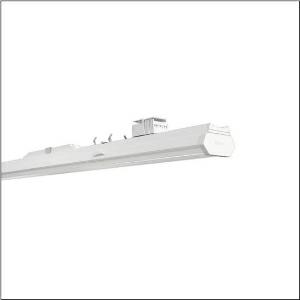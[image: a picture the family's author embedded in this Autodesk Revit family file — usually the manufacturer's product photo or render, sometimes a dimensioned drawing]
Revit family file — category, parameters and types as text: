
# Revit family: licross_21_protected_ho_52tp11dn4axs
name_source: partatom
category: Lighting Fixtures
units: mm (PartAtom-declared; Revit-internal decimal feet)

## family parameters
Cut with Voids When Loaded = No
Host = Face
Light Source = No
Part Type = Normal
Room Calculation Point = No
Round Connector Dimension = Use Diameter
Shared = No

## types (1)
- --- (1 x LED, 10000 lm, 55.1 W, 4000K)
    Apparent Load = 55 VA
    CIE Flux Codes = 84 94 98 99 100
    Color Rendering = 80
    Color Temperature = 4000K
    Default Elevation = 1800 mm
    Description = Licross 21 Protected HO, luminaire insert, of sheet steel, galvanised, coil coated, white, length: 1.500mm, width: 90mm, height: 103mm, LED rated luminous flux: 10.000lm, light colour: 840, SDCM (Standard Deviation of Colour Matching)MacAdam ≤ 3 SDCM (initial), control gear: DALI 2, with plug, 5-pole, with phase selection, mains connection: 220..240V, AC, 50/60Hz, rated input power: 55W, internal wiring halogen-free, primary light control with lens, of plastic, primary optical cover: cover, of PMMA, light emission: direct distribution, primary light characteristic: symmetric, protection rating (complete): IP64, insulation class (complete): insulation class I (protective earthing), certification: CE, ENEC, VDE, UKCA, protection symbol: D if used in an environment with conductive dust loads with corresponding accessories, impact resistance: IK06, permissible ambient temperature for indoor applications: -25..+45°C, corresponds to IFS (International Featured Standards) requirements for safety and quality in the food industry, reducing of maximum allowable ambient temperature of 5°C with ceiling mounting, LABS conformity tested according to VDMA 24364:2018-05, The light source and the operating device comply with the requirements of the Ecodesign Regulation (EU) 2019/2020 and are replaceable in accordance with this regulation, packaging unit: 1 piece
    Height = 92 mm
    Lamp = 1 x LED
    Lamp Light Flux = 10000 lm
    Lamp Power = 55.1 W
    Lamp count = 1
    Length = 1500 mm
    Luminous efficacy = 181 lm/W
    Manufacturer = Siteco
    ModVariant = No
    Model = 52TP11DN4AXS
    Mounting Place = Ceiling
    Mounting Type = Pendant
    Number of Poles = 1
    OnlyDefault = Yes
    Power Factor = 1
    Product Name = Licross 21 Protected HO
    Product group = luminaire insert | ceiling pendant
    ProductGroupID = 901
    Protection Class = Protection class I
    Protection Degree = IP 64
    RLX_Detail_Level = 1
    RLX_Emergency_Light_Flux = 0 lm
    RLX_Emergency_Type = 0
    RLX_Emergency_Type_DB = No
    RlxData = <blob elided: 24377 chars, md5=d9ce4f86>
    Socket = socket
    Standby Power = 0 W
    System Light Flux = 10000 lm
    System Power = 55 W
    Type Comments = factory setting: luminous flux: 100 % | dim-lin: 254 | 316 mA
    Type Image = l_1256148.jpg
    URL = http://relux.com
    VarID = @adj_128551
    Voltage = 0 V
    Weight = 0.00 kg
    Width = 88 mm

## geometry (parser evidence)
native form markers: Blend x4, Sweep x10
no freeform markers — native parametric forms only
